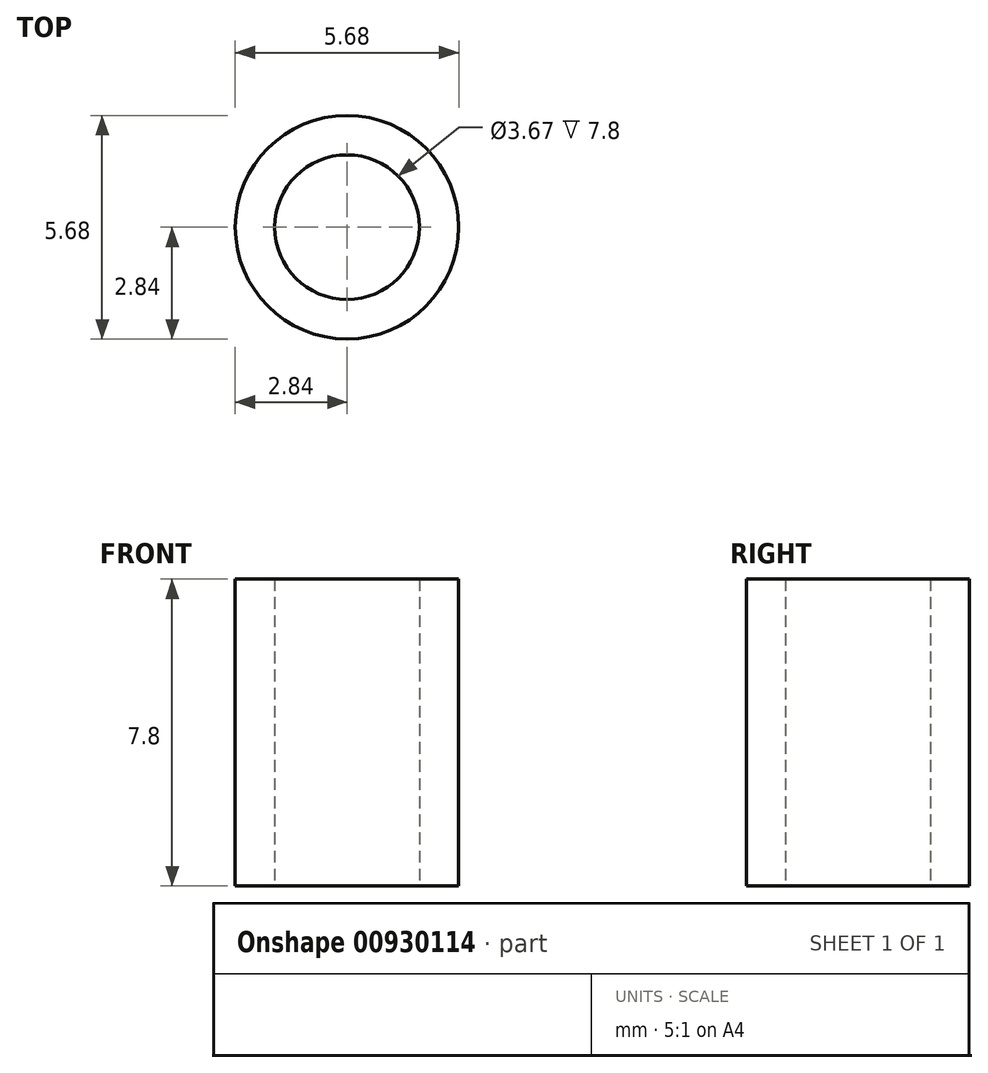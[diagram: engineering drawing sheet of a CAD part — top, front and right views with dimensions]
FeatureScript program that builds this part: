
annotation { "Feature Type Name" : "Feature", "Feature Type Description" : "" }
export const myFeature = defineFeature(function(context is Context, id is Id, definition is map)
    precondition{}
    {
        {
            var Q0;
            Q0=qCreatedBy(makeId("Top.planeOp"),FACE);
            var sketch = newSketch(context, id + "F0", { "sketchPlane" : qUnion([Q0])});
            skCircle(sketch, "E0", {"center": v(0, 0) * mm, "radius": 1.84 * mm});
            skCircle(sketch, "E1", {"center": v(0, 0) * mm, "radius": 2.84 * mm});
            skSolve(sketch);
        }
        {
            var Q0;
            Q0=makeQuery(id+"F0.imprint","IMPRINT",FACE,{"disambiguationData":[TD([[makeQuery(id+"F0.imprint","IMPRINT",EDGE,{"derivedFrom":sQuery(id+"F0.wireOp",EDGE,"E0")}),-1.0]])]});
            extrude(context, id + "F1", {"entities" : qUnion([Q0]), "depth" : 7.8 * mm, "offsetDistance" : 25 * mm});
        }
    });
